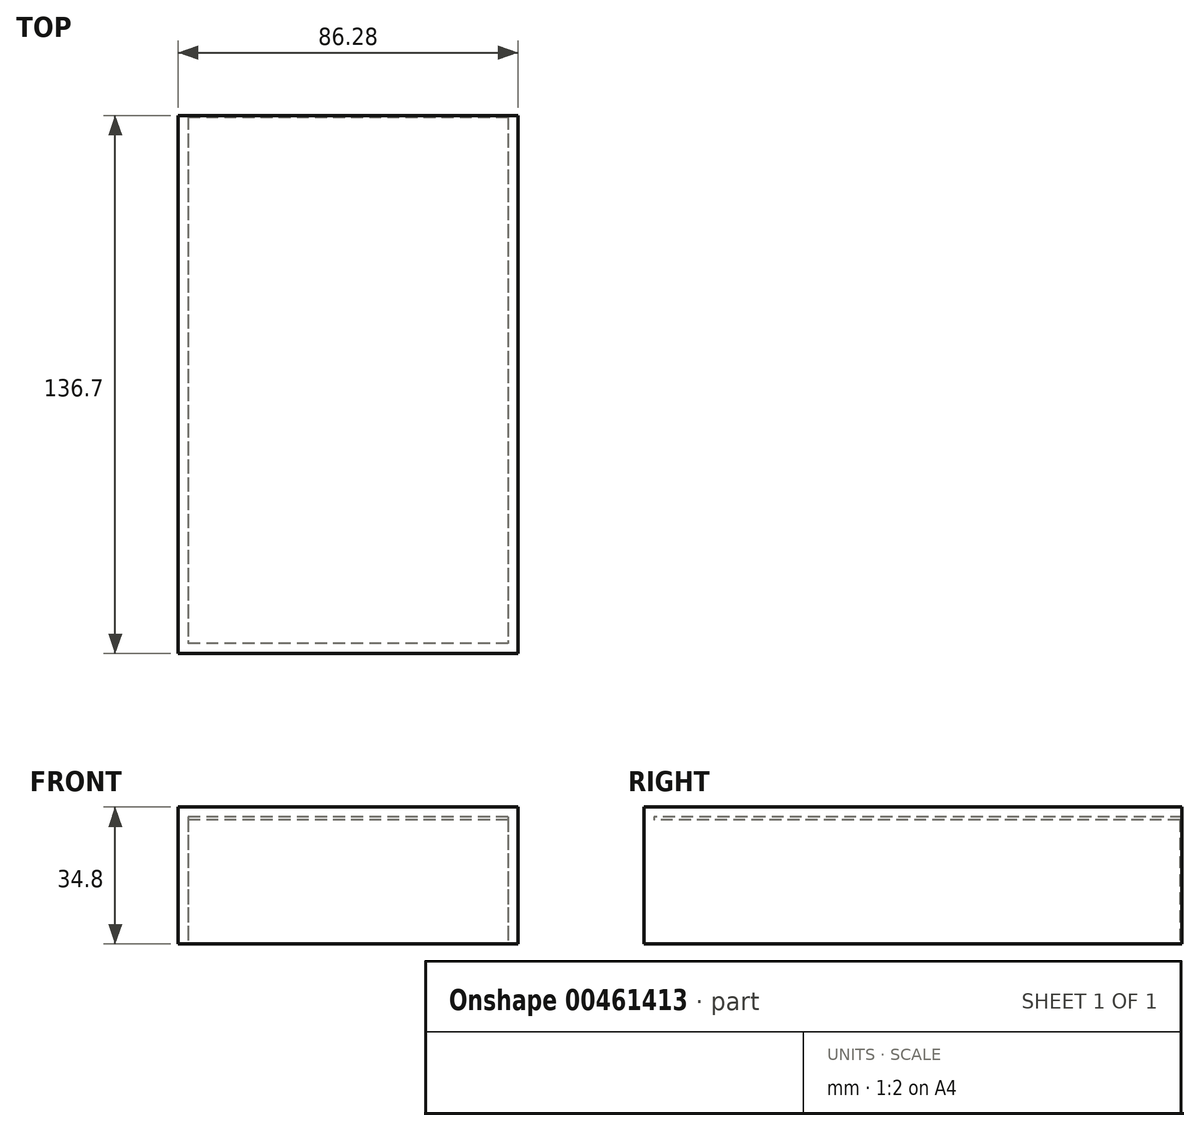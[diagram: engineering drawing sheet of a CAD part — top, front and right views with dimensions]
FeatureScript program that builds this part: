
annotation { "Feature Type Name" : "Feature", "Feature Type Description" : "" }
export const myFeature = defineFeature(function(context is Context, id is Id, definition is map)
    precondition{}
    {
        {
            var Q0;
            Q0=qCreatedBy(makeId("Top.planeOp"),FACE);
            var sketch = newSketch(context, id + "F0", { "sketchPlane" : qUnion([Q0])});
            skLineSegment(sketch, "E0.bottom", {"start": v(43.14, 68.35) * mm, "end": v(-43.14, 68.35) * mm});
            skLineSegment(sketch, "E0.top", {"start": v(43.14, -68.35) * mm, "end": v(-43.14, -68.35) * mm});
            skLineSegment(sketch, "E0.left", {"start": v(43.14, 68.35) * mm, "end": v(43.14, -68.35) * mm});
            skLineSegment(sketch, "E0.right", {"start": v(-43.14, 68.35) * mm, "end": v(-43.14, -68.35) * mm});
            skPoint(sketch, "E0.middle", {"position": v(0, 0) * mm});
            skSolve(sketch);
        }
        {
            var Q0;
            Q0 = qSketchRegion(id + "F0", true);
            extrude(context, id + "F1", {"entities" : qUnion([Q0]), "depth" : 34.8 * mm});
        }
        {
            var Q0;
            Q0=makeQuery(id+"F1.opExtrude","CAP_FACE",FACE,{"disambiguationData":[OSD([sQuery(id+"F0.wireOp",EDGE,"E0.bottom"),sQuery(id+"F0.wireOp",EDGE,"E0.top"),sQuery(id+"F0.wireOp",EDGE,"E0.left"),sQuery(id+"F0.wireOp",EDGE,"E0.right")])],"isStart":true});
            var Q1;
            Q1=makeQuery(id+"F1.opExtrude","SWEPT_FACE",FACE,{"disambiguationData":[OSD([sQuery(id+"F0.wireOp",EDGE,"E0.bottom")])]});
            shell(context, id + "F2", {"entities" : qUnion([Q0, Q1]), "thickness" : 2.54 * mm});
        }
        {
            var Q0;
            Q0=qCreatedBy(makeId("Top.planeOp"),FACE);
            var sketch = newSketch(context, id + "F3", { "sketchPlane" : qUnion([Q0])});
            skLineSegment(sketch, "E1.bottom", {"start": v(42.26, 67.77) * mm, "end": v(-42.26, 67.77) * mm});
            skLineSegment(sketch, "E1.top", {"start": v(42.26, -67.77) * mm, "end": v(-42.26, -67.77) * mm});
            skLineSegment(sketch, "E1.left", {"start": v(42.26, 67.77) * mm, "end": v(42.26, -67.77) * mm});
            skLineSegment(sketch, "E1.right", {"start": v(-42.26, 67.77) * mm, "end": v(-42.26, -67.77) * mm});
            skPoint(sketch, "E1.middle", {"position": v(0, 0) * mm});
            skSolve(sketch);
        }
        {
            var Q0;
            Q0 = qSketchRegion(id + "F3", true);
            extrude(context, id + "F4", {"entities" : qUnion([Q0]), "operationType" : NewBodyOperationType.ADD, "depth" : 31.5 * mm});
        }
    });
